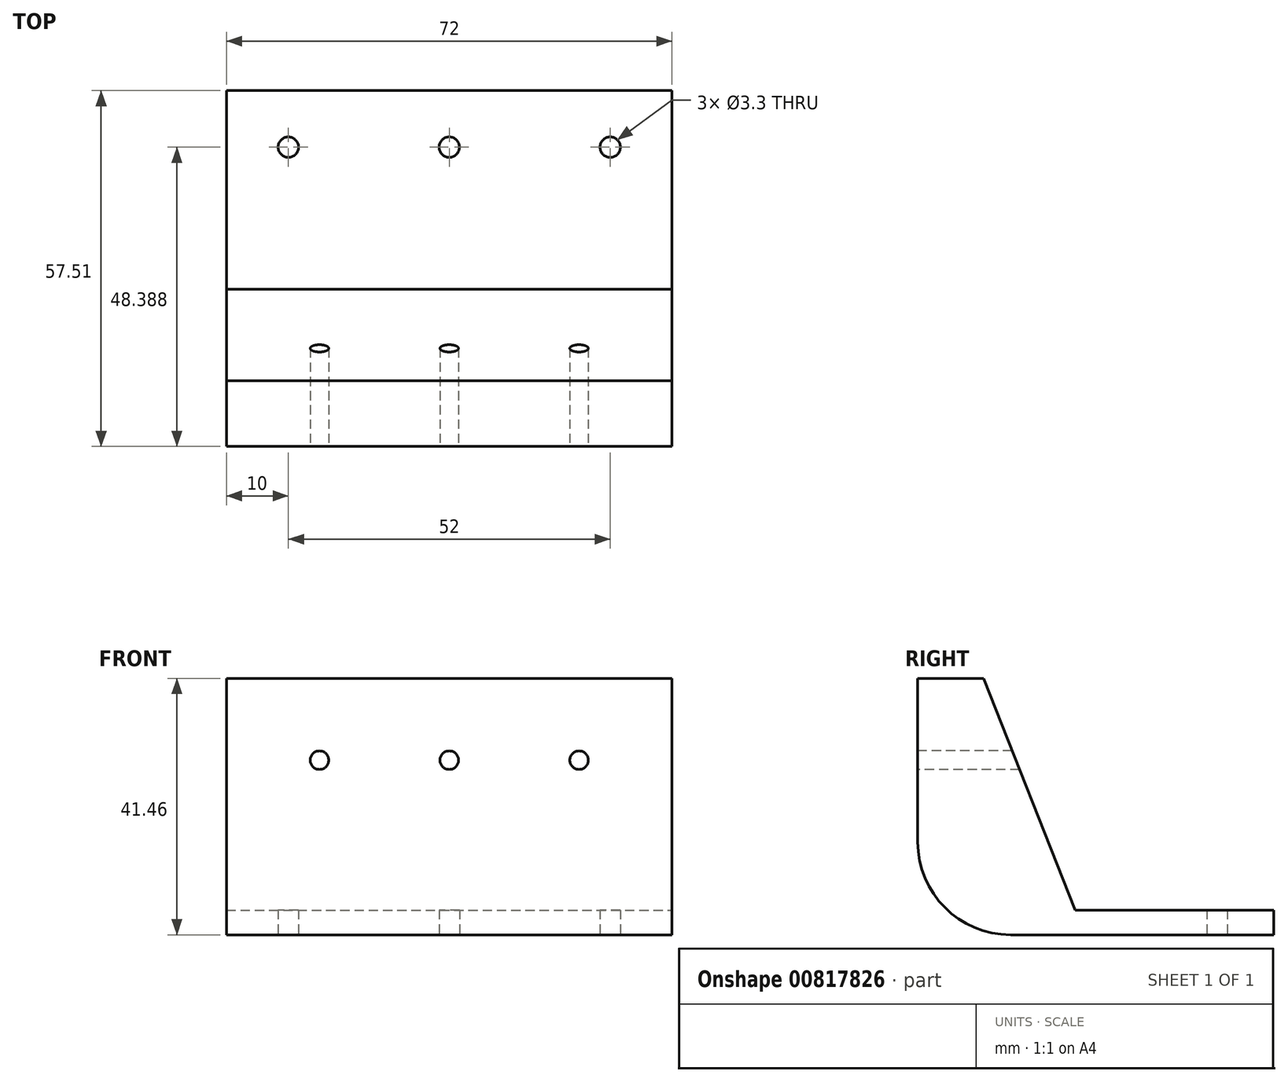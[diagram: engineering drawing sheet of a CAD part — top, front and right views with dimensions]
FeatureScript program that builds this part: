
annotation { "Feature Type Name" : "Feature", "Feature Type Description" : "" }
export const myFeature = defineFeature(function(context is Context, id is Id, definition is map)
    precondition{}
    {
        {
            var Q0;
            Q0=qCreatedBy(makeId("Top.planeOp"),FACE);
            var sketch = newSketch(context, id + "F0", { "sketchPlane" : qUnion([Q0])});
            skLineSegment(sketch, "E0.bottom", {"start": v(36, 22.5) * mm, "end": v(-36, 22.5) * mm});
            skLineSegment(sketch, "E0.top", {"start": v(36, -22.5) * mm, "end": v(-36, -22.5) * mm});
            skLineSegment(sketch, "E0.left", {"start": v(36, 22.5) * mm, "end": v(36, -22.5) * mm});
            skLineSegment(sketch, "E0.right", {"start": v(-36, 22.5) * mm, "end": v(-36, -22.5) * mm});
            skPoint(sketch, "E0.middle", {"position": v(0, 0) * mm});
            skPoint(sketch, "E1", {"position": v(0, 13.38) * mm});
            skPoint(sketch, "E2", {"position": v(-26, 13.38) * mm});
            skPoint(sketch, "E3.MirrorP", {"position": v(26, 13.38) * mm});
            skSolve(sketch);
        }
        {
            var Q0;
            Q0=makeQuery(id+"F0.imprint","IMPRINT",FACE,{"disambiguationData":[TD([[makeQuery(id+"F0.imprint","IMPRINT",EDGE,{"derivedFrom":sQuery(id+"F0.wireOp",EDGE,"E0.bottom")}),1.0]])]});
            extrude(context, id + "F1", {"entities" : qUnion([Q0]), "depth" : 4 * mm, "offsetDistance" : 25 * mm});
        }
        {
            var Q0;
            Q0=sQuery(id+"F0.wireOp",VERTEX,"E2");
            var Q1;
            Q1=sQuery(id+"F0.wireOp",VERTEX,"E1");
            var Q2;
            Q2=sQuery(id+"F0.wireOp",VERTEX,"E3.MirrorP");
            var Q3;
            Q3=makeQuery(id+"F1.opExtrude","SWEPT_BODY",BODY,{"disambiguationData":[OSD([sQuery(id+"F0.wireOp",EDGE,"E0.bottom"),sQuery(id+"F0.wireOp",EDGE,"E0.top"),sQuery(id+"F0.wireOp",EDGE,"E0.left"),sQuery(id+"F0.wireOp",EDGE,"E0.right")])]});
            hole(context, id + "F2", {"style" : HoleStyle.SIMPLE, "endStyle" : HoleEndStyle.BLIND, "oppositeDirection" : true, "standardTappedOrClearance" : lookupTablePath({ "standard" : "ISO", "fit" : "Normal", "size" : "M3", "type" : "Clearance" }), "standardBlindInLast" : lookupTablePath({ "fit" : "Standard", "standard" : "ISO", "size" : "M3", "type" : "Clearance" }), "holeDiameter" : 3.3 * mm, "majorDiameter" : 5 * mm, "holeDepth" : 8 * mm, "isTappedThrough" : true, "tappedDepth" : 12 * mm, "tapClearance" : 3, "startFromSketch" : true, "locations" : qUnion([Q0, Q1, Q2]), "scope" : qUnion([Q3])});
        }
        {
            var Q0;
            Q0=makeQuery(id+"F1.opExtrude","SWEPT_FACE",FACE,{"disambiguationData":[OSD([sQuery(id+"F0.wireOp",EDGE,"E0.left")])]});
            var sketch = newSketch(context, id + "F3", { "sketchPlane" : qUnion([Q0])});
            skLineSegment(sketch, "E4", {"start": v(-9.58, 4) * mm, "end": v(-24.38, 41.46) * mm});
            skLineSegment(sketch, "E5", {"start": v(-24.38, 41.46) * mm, "end": v(-35.01, 41.46) * mm});
            skLineSegment(sketch, "E6", {"start": v(-35.01, 41.46) * mm, "end": v(-35.01, 0) * mm});
            skLineSegment(sketch, "E7", {"start": v(-35.01, 0) * mm, "end": v(-8.44, 0) * mm});
            skSolve(sketch);
        }
        {
            var Q0;
            {var subQ4=sQuery(id+"F3.wireOp",EDGE,"E4");Q0=makeQuery(id+"F3.imprint","IMPRINT",FACE,{"disambiguationData":[TD([[makeQuery(id+"F3.imprint","IMPRINT",EDGE,{"derivedFrom":subQ4}),1.0]])]});}
            extrude(context, id + "F4", {"entities" : qUnion([Q0]), "operationType" : NewBodyOperationType.ADD, "oppositeDirection" : true, "depth" : 72 * mm, "offsetDistance" : 25 * mm});
        }
        {
            var Q0;
            Q0=makeQuery(id+"F4.opExtrude","SWEPT_EDGE",EDGE,{"disambiguationData":[OSD([sQuery(id+"F3.wireOp",EDGE,"E6"),sQuery(id+"F3.wireOp",EDGE,"E7")])]});
            var Q1;
            Q1=makeQuery(id+"F4.opExtrude","SWEPT_EDGE",EDGE,{"disambiguationData":[OSD([sQuery(id+"F0.wireOp",EDGE,"E0.left"),sQuery(id+"F3.wireOp",EDGE,"E4")])]});
            fillet(context, id + "F5", {"entities" : qUnion([Q0, Q1]), "radius" : 15 * mm, "tangentPropagation" : true, "allowEdgeOverflow" : false});
        }
        {
            var Q0;
            Q0=makeQuery(id+"F4.opExtrude","SWEPT_FACE",FACE,{"disambiguationData":[OSD([sQuery(id+"F3.wireOp",EDGE,"E6")])]});
            var sketch = newSketch(context, id + "F6", { "sketchPlane" : qUnion([Q0])});
            skLineSegment(sketch, "E8", {"start": v(-36, 28.23) * mm, "end": v(36, 28.23) * mm, "construction": true});
            skPoint(sketch, "E9", {"position": v(-20.97, 28.23) * mm});
            skPoint(sketch, "E10.MirrorP", {"position": v(20.97, 28.23) * mm});
            skPoint(sketch, "E11", {"position": v(0, 28.23) * mm});
            skSolve(sketch);
        }
        {
            var Q0;
            Q0=sQuery(id+"F6.wireOp",VERTEX,"E9");
            var Q1;
            Q1=sQuery(id+"F6.wireOp",VERTEX,"E10.MirrorP");
            var Q2;
            Q2=sQuery(id+"F6.wireOp",VERTEX,"E11");
            var Q3;
            Q3=makeQuery(id+"F1.opExtrude","SWEPT_BODY",BODY,{"disambiguationData":[OSD([sQuery(id+"F0.wireOp",EDGE,"E0.bottom"),sQuery(id+"F0.wireOp",EDGE,"E0.top"),sQuery(id+"F0.wireOp",EDGE,"E0.left"),sQuery(id+"F0.wireOp",EDGE,"E0.right")])]});
            hole(context, id + "F7", {"style" : HoleStyle.SIMPLE, "endStyle" : HoleEndStyle.BLIND, "holeDiameter" : 3 * mm, "majorDiameter" : 5 * mm, "holeDepth" : 25 * mm, "isTappedThrough" : true, "tappedDepth" : 12 * mm, "tapClearance" : 3, "startFromSketch" : true, "locations" : qUnion([Q0, Q1, Q2]), "scope" : qUnion([Q3])});
        }
    });
